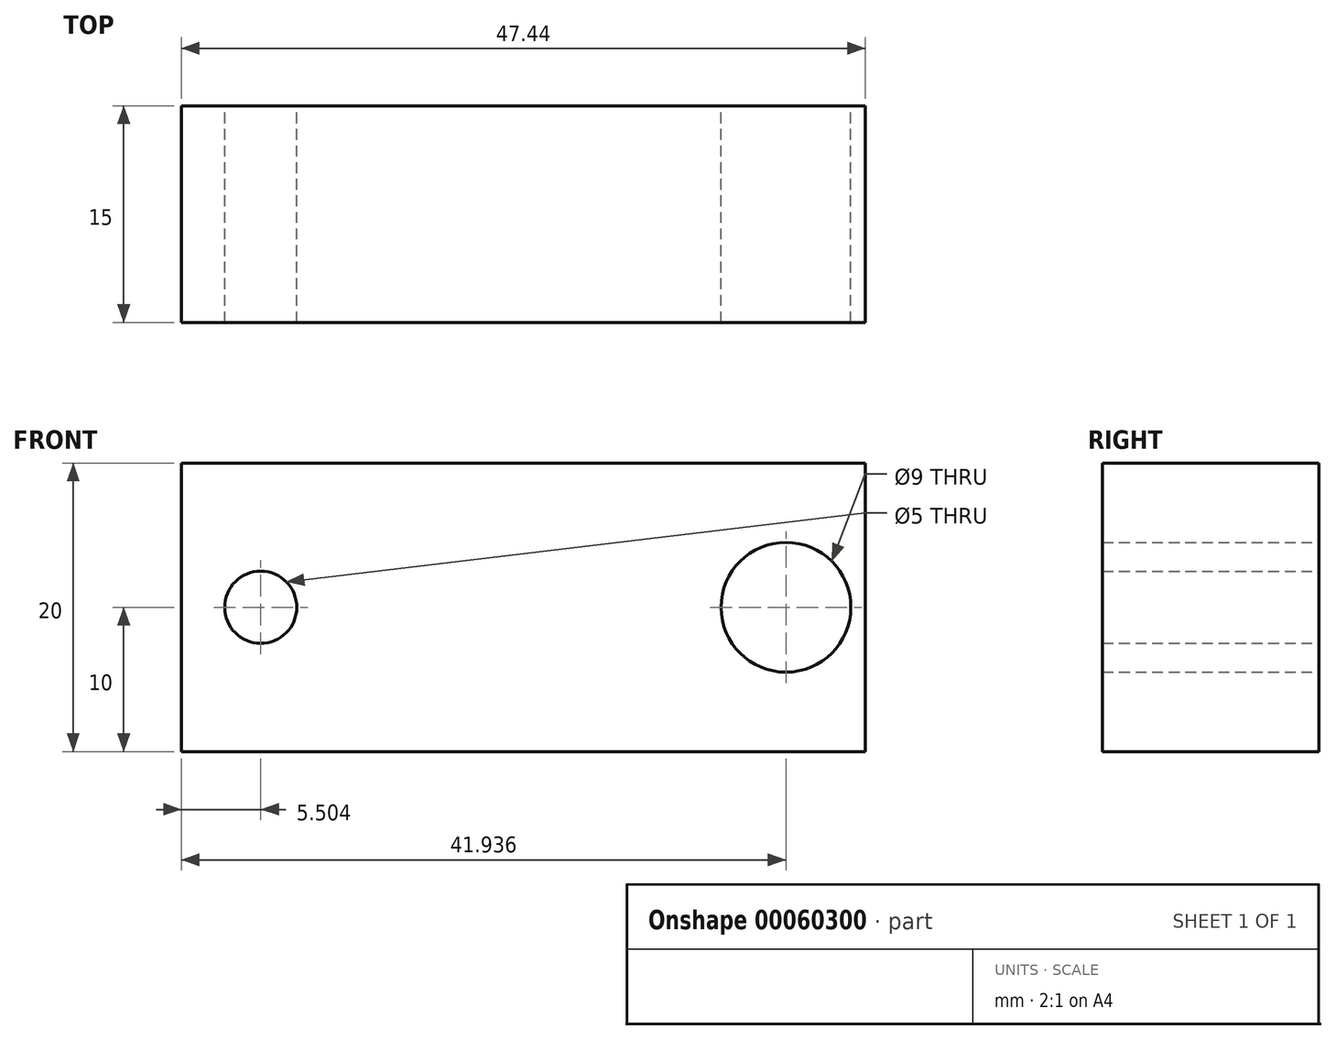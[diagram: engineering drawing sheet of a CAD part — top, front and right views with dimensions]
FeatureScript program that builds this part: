
annotation { "Feature Type Name" : "Feature", "Feature Type Description" : "" }
export const myFeature = defineFeature(function(context is Context, id is Id, definition is map)
    precondition{}
    {
        {
            var Q0;
            Q0=qCreatedBy(makeId("Front.planeOp"),FACE);
            var sketch = newSketch(context, id + "F0", { "sketchPlane" : qUnion([Q0])});
            skLineSegment(sketch, "E0.bottom", {"start": v(-23.72, 10) * mm, "end": v(23.72, 10) * mm});
            skLineSegment(sketch, "E0.top", {"start": v(-23.72, -10) * mm, "end": v(23.72, -10) * mm});
            skLineSegment(sketch, "E0.left", {"start": v(-23.72, 10) * mm, "end": v(-23.72, -10) * mm});
            skLineSegment(sketch, "E0.right", {"start": v(23.72, 10) * mm, "end": v(23.72, -10) * mm});
            skLineSegment(sketch, "E1", {"start": v(0, 10) * mm, "end": v(0, -10) * mm, "construction": true});
            skLineSegment(sketch, "E2", {"start": v(-23.72, 0) * mm, "end": v(23.72, 0) * mm, "construction": true});
            skCircle(sketch, "E3", {"center": v(-18.22, 0) * mm, "radius": 2.5 * mm});
            skCircle(sketch, "E4", {"center": v(-18.22, 0) * mm, "radius": 4.5 * mm});
            skCircle(sketch, "E5.MirrorC", {"center": v(18.22, 0) * mm, "radius": 4.5 * mm});
            skCircle(sketch, "E6.MirrorC", {"center": v(18.22, 0) * mm, "radius": 2.5 * mm});
            skSolve(sketch);
        }
        {
            var Q0;
            Q0=qSketchRegion(id+"F0",true);
            extrude(context, id + "F1", {"entities" : qUnion([Q0]), "depth" : 15 * mm});
        }
        {
            var Q0;
            Q0=makeQuery(id+"F1.opExtrude","SWEPT_FACE",FACE,{"disambiguationData":[OSD([sQuery(id+"F0.wireOp",EDGE,"E0.bottom")])]});
            var sketch = newSketch(context, id + "F2", { "sketchPlane" : qUnion([Q0])});
            skLineSegment(sketch, "E7", {"start": v(0, 0) * mm, "end": v(0, -15) * mm, "construction": true});
            skCircle(sketch, "E8", {"center": v(0, -15) * mm, "radius": 7.05 * mm});
            skSolve(sketch);
        }
        {
            var Q0;
            Q0=qSketchRegion(id+"F2",true);
            extrude(context, id + "F3", {"entities" : qUnion([Q0]), "operationType" : NewBodyOperationType.REMOVE, "oppositeDirection" : true, "depth" : 25 * mm});
        }
        {
            var Q0;
            {var subQ0=sQuery(id+"F0.wireOp",EDGE,"E0.bottom");var subQ1=sQuery(id+"F0.wireOp",EDGE,"E0.top");var subQ2=sQuery(id+"F0.wireOp",EDGE,"E0.left");Q0=makeQuery(id+"F3.boolean.opBoolean","SPLIT",FACE,{"disambiguationData":[TD([makeQuery(id+"F1.opExtrude","SWEPT_FACE",FACE,{"disambiguationData":[OSD([subQ2])]})])],"derivedFrom":makeQuery(id+"F1.opExtrude","CAP_FACE",FACE,{"disambiguationData":[OSD([subQ0,subQ1,subQ2,sQuery(id+"F0.wireOp",EDGE,"E0.right")])],"isStart":false})});}
            var sketch = newSketch(context, id + "F4", { "sketchPlane" : qUnion([Q0])});
            skLineSegment(sketch, "E9", {"start": v(0, 10.04) * mm, "end": v(0, -9.96) * mm});
            skArc(sketch, "E10", {"start": v(-7.05, 10) * mm, "mid": v(-12.24, 0) * mm, "end": v(-7.05, -10) * mm});
            skSolve(sketch);
        }
        {
            var Q0;
            Q0=makeQuery(id+"F4.imprint","IMPRINT",FACE,{"disambiguationData":[TD([[makeQuery(id+"F4.imprint","IMPRINT",EDGE,{"derivedFrom":sQuery(id+"F4.wireOp",EDGE,"E10")}),1.0]])]});
            var Q1;
            Q1=sQuery(id+"F4.wireOp",EDGE,"E9");
            revolve(context, id + "F5", {"operationType" : NewBodyOperationType.REMOVE, "entities" : qUnion([Q0]), "axis" : qUnion([Q1]), "revolveType" : RevolveType.FULL, "oppositeDirection" : true});
        }
        {
            var Q0;
            {var subQ0=sQuery(id+"F0.wireOp",EDGE,"E0.bottom");var subQ1=sQuery(id+"F0.wireOp",EDGE,"E0.top");var subQ2=sQuery(id+"F0.wireOp",EDGE,"E0.right");Q0=makeQuery(id+"F3.boolean.opBoolean","SPLIT",FACE,{"disambiguationData":[TD([makeQuery(id+"F1.opExtrude","SWEPT_FACE",FACE,{"disambiguationData":[OSD([subQ2])]})])],"derivedFrom":makeQuery(id+"F1.opExtrude","CAP_FACE",FACE,{"disambiguationData":[OSD([subQ0,subQ1,sQuery(id+"F0.wireOp",EDGE,"E0.left"),subQ2])],"isStart":false})});}
            var sketch = newSketch(context, id + "F6", { "sketchPlane" : qUnion([Q0])});
            skLineSegment(sketch, "E11", {"start": v(0, 10.25) * mm, "end": v(0, 10) * mm, "construction": true});
            skLineSegment(sketch, "E12.bottom", {"start": v(2.5, 10) * mm, "end": v(0, 10) * mm});
            skLineSegment(sketch, "E12.top", {"start": v(2.5, -10.08) * mm, "end": v(0, -10.08) * mm});
            skLineSegment(sketch, "E13", {"start": v(2.5, 10) * mm, "end": v(2.5, -10.08) * mm});
            skLineSegment(sketch, "E14.MirrorCS", {"start": v(-2.5, 10) * mm, "end": v(-2.5, -10.08) * mm});
            skLineSegment(sketch, "E15", {"start": v(-2.5, 10) * mm, "end": v(2.5, 10) * mm});
            skLineSegment(sketch, "E16", {"start": v(-2.5, -10.08) * mm, "end": v(2.5, -10.08) * mm});
            skSolve(sketch);
        }
        {
            var Q0;
            Q0=qSketchRegion(id+"F6",true);
            extrude(context, id + "F7", {"entities" : qUnion([Q0]), "operationType" : NewBodyOperationType.REMOVE, "oppositeDirection" : true, "depth" : 13.25 * mm});
        }
        {
            var Q0;
            Q0=makeQuery(id+"F7.boolean.opBoolean","COPY",EDGE,{"derivedFrom":makeQuery(id+"F7.opExtrude","CAP_EDGE",EDGE,{"disambiguationData":[OSD([sQuery(id+"F6.wireOp",EDGE,"E13")])],"isStart":false})});
            var Q1;
            Q1=makeQuery(id+"F7.boolean.opBoolean","COPY",EDGE,{"derivedFrom":makeQuery(id+"F7.opExtrude","CAP_EDGE",EDGE,{"disambiguationData":[OSD([sQuery(id+"F6.wireOp",EDGE,"E14.MirrorCS")])],"isStart":false})});
            fillet(context, id + "F8", {"entities" : qUnion([Q0, Q1]), "radius" : 1 * mm, "tangentPropagation" : true, "rho" : 0.7, "crossSection" : FilletCrossSection.CONIC, "allowEdgeOverflow" : false});
        }
        {
            var Q0;
            Q0=makeQuery(id+"F0.imprint","IMPRINT",FACE,{"disambiguationData":[TD([[makeQuery(id+"F0.imprint","IMPRINT",EDGE,{"derivedFrom":sQuery(id+"F0.wireOp",EDGE,"E3")}),-1.0]])]});
            var Q1;
            Q1=makeQuery(id+"F0.imprint","IMPRINT",FACE,{"disambiguationData":[TD([[makeQuery(id+"F0.imprint","IMPRINT",EDGE,{"derivedFrom":sQuery(id+"F0.wireOp",EDGE,"E5.MirrorC")}),-1.0]])]});
            extrude(context, id + "F9", {"entities" : qUnion([Q0, Q1]), "operationType" : NewBodyOperationType.ADD, "depth" : 15 * mm});
        }
    });
